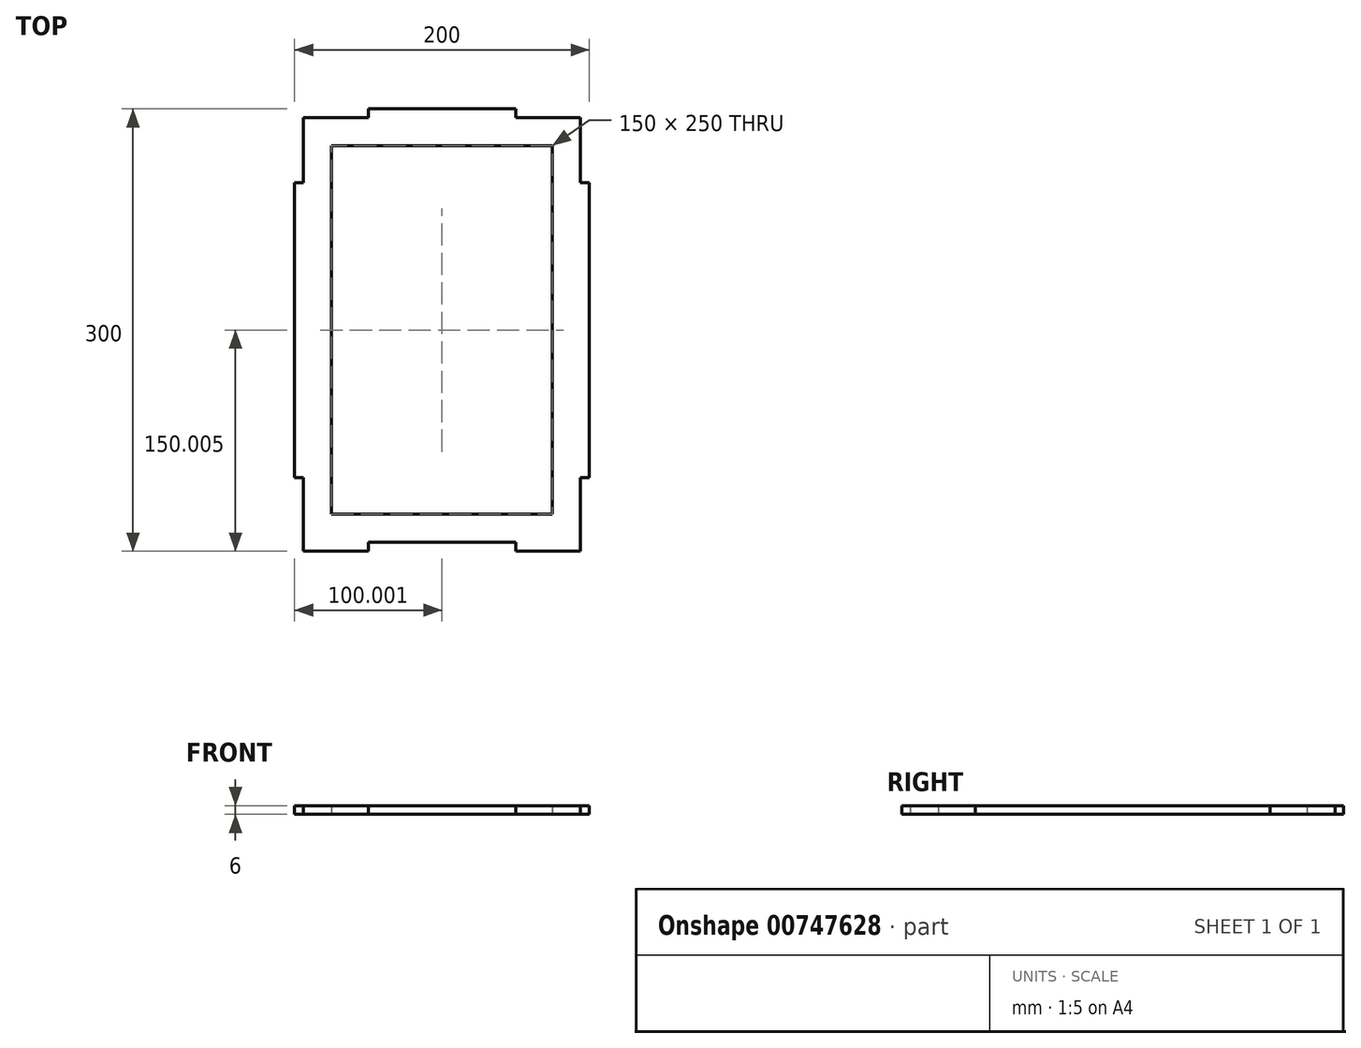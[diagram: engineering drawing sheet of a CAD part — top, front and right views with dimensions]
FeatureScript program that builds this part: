
annotation { "Feature Type Name" : "Feature", "Feature Type Description" : "" }
export const myFeature = defineFeature(function(context is Context, id is Id, definition is map)
    precondition{}
    {
        {
            var Q0;
            Q0=qCreatedBy(makeId("Top.planeOp"),FACE);
            var sketch = newSketch(context, id + "F0", { "sketchPlane" : qUnion([Q0])});
            skLineSegment(sketch, "E0.bottom", {"start": v(-78.62, 212.4) * mm, "end": v(-34.62, 212.4) * mm});
            skLineSegment(sketch, "E0.top", {"start": v(-78.62, -81.6) * mm, "end": v(109.38, -81.6) * mm});
            skLineSegment(sketch, "E0.left", {"start": v(-78.62, 212.4) * mm, "end": v(-78.62, 168.4) * mm});
            skLineSegment(sketch, "E0.right", {"start": v(109.38, 212.4) * mm, "end": v(109.38, 168.4) * mm});
            skLineSegment(sketch, "E1.top", {"start": v(-34.62, 218.4) * mm, "end": v(65.38, 218.4) * mm});
            skLineSegment(sketch, "E1.left", {"start": v(-34.62, 212.4) * mm, "end": v(-34.62, 218.4) * mm});
            skLineSegment(sketch, "E1.right", {"start": v(65.38, 212.4) * mm, "end": v(65.38, 218.4) * mm});
            skLineSegment(sketch, "E2.trimOffspring", {"start": v(65.38, 212.4) * mm, "end": v(109.38, 212.4) * mm});
            skLineSegment(sketch, "E3.bottom", {"start": v(-78.62, 168.4) * mm, "end": v(-84.62, 168.4) * mm});
            skLineSegment(sketch, "E3.top", {"start": v(-78.62, -31.6) * mm, "end": v(-84.62, -31.6) * mm});
            skLineSegment(sketch, "E3.right", {"start": v(-84.62, 168.4) * mm, "end": v(-84.62, -31.6) * mm});
            skLineSegment(sketch, "E4.bottom", {"start": v(109.38, 168.4) * mm, "end": v(115.38, 168.4) * mm});
            skLineSegment(sketch, "E4.top", {"start": v(109.38, -31.6) * mm, "end": v(115.38, -31.6) * mm});
            skLineSegment(sketch, "E4.right", {"start": v(115.38, 168.4) * mm, "end": v(115.38, -31.6) * mm});
            skLineSegment(sketch, "E5.trimOffspring", {"start": v(109.38, -31.6) * mm, "end": v(109.38, -81.6) * mm});
            skLineSegment(sketch, "E6.trimOffspring", {"start": v(-78.62, -31.6) * mm, "end": v(-78.62, -81.6) * mm});
            skLineSegment(sketch, "E7.bottom", {"start": v(-59.62, 193.4) * mm, "end": v(90.38, 193.4) * mm});
            skLineSegment(sketch, "E7.top", {"start": v(-59.62, -56.6) * mm, "end": v(90.38, -56.6) * mm});
            skLineSegment(sketch, "E7.left", {"start": v(-59.62, 193.4) * mm, "end": v(-59.62, -56.6) * mm});
            skLineSegment(sketch, "E7.right", {"start": v(90.38, 193.4) * mm, "end": v(90.38, -56.6) * mm});
            skLineSegment(sketch, "E8", {"start": v(-59.62, 68.4) * mm, "end": v(-84.62, 68.4) * mm, "construction": true});
            skLineSegment(sketch, "E9", {"start": v(15.38, 193.4) * mm, "end": v(15.38, 218.4) * mm, "construction": true});
            skLineSegment(sketch, "E10", {"start": v(-34.62, -81.6) * mm, "end": v(-34.62, -75.6) * mm});
            skLineSegment(sketch, "E11", {"start": v(-34.62, -75.6) * mm, "end": v(65.38, -75.6) * mm});
            skLineSegment(sketch, "E12", {"start": v(65.38, -75.6) * mm, "end": v(65.38, -81.6) * mm});
            skLineSegment(sketch, "E13", {"start": v(15.38, -75.6) * mm, "end": v(15.38, -81.6) * mm, "construction": true});
            skSolve(sketch);
        }
        {
            var Q0;
            Q0=makeQuery(id+"F0.imprint","IMPRINT",FACE,{"disambiguationData":[TD([[makeQuery(id+"F0.imprint","IMPRINT",EDGE,{"derivedFrom":sQuery(id+"F0.wireOp",EDGE,"E0.bottom")}),-1.0]])]});
            extrude(context, id + "F1", {"entities" : qUnion([Q0]), "depth" : 6 * mm, "offsetDistance" : 25.4 * mm});
        }
    });
